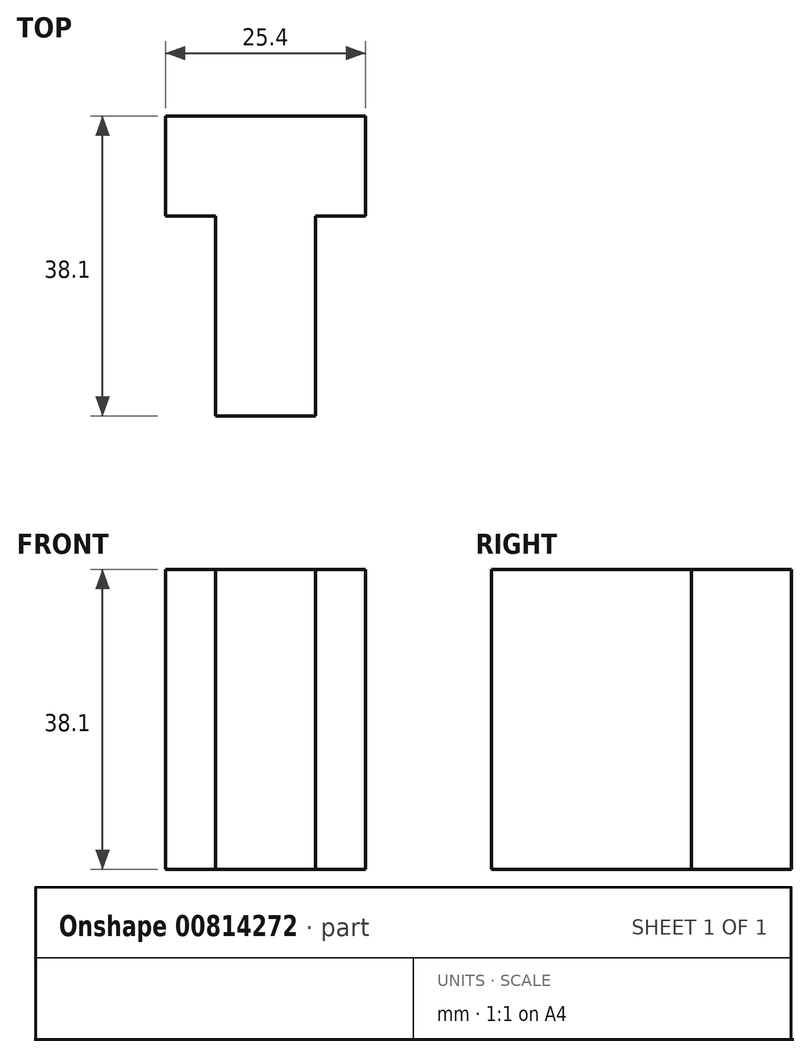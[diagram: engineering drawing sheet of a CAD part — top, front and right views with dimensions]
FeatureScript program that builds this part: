
annotation { "Feature Type Name" : "Feature", "Feature Type Description" : "" }
export const myFeature = defineFeature(function(context is Context, id is Id, definition is map)
    precondition{}
    {
        {
            var Q0;
            Q0=qCreatedBy(makeId("Top.planeOp"),FACE);
            var sketch = newSketch(context, id + "F0", { "sketchPlane" : qUnion([Q0])});
            skLineSegment(sketch, "E0", {"start": v(-10.03, 39.47) * mm, "end": v(15.37, 39.47) * mm});
            skLineSegment(sketch, "E1", {"start": v(-10.03, 39.47) * mm, "end": v(-10.03, 26.77) * mm});
            skLineSegment(sketch, "E2", {"start": v(15.37, 39.47) * mm, "end": v(15.37, 26.77) * mm});
            skLineSegment(sketch, "E3", {"start": v(-10.03, 26.77) * mm, "end": v(-3.68, 26.77) * mm});
            skLineSegment(sketch, "E4", {"start": v(15.37, 26.77) * mm, "end": v(9.02, 26.77) * mm});
            skLineSegment(sketch, "E5", {"start": v(-3.68, 26.77) * mm, "end": v(-3.68, 1.37) * mm});
            skLineSegment(sketch, "E6", {"start": v(9.02, 26.77) * mm, "end": v(9.02, 1.37) * mm});
            skLineSegment(sketch, "E7", {"start": v(-3.68, 1.37) * mm, "end": v(9.02, 1.37) * mm});
            skLineSegment(sketch, "E8", {"start": v(-90.62, 9.05) * mm, "end": v(-85.95, 4.96) * mm});
            skSolve(sketch);
        }
        {
            var Q0;
            Q0 = qSketchRegion(id + "F0", true);
            extrude(context, id + "F1", {"entities" : qUnion([Q0]), "depth" : 38.1 * mm, "offsetDistance" : 25.4 * mm});
        }
    });
